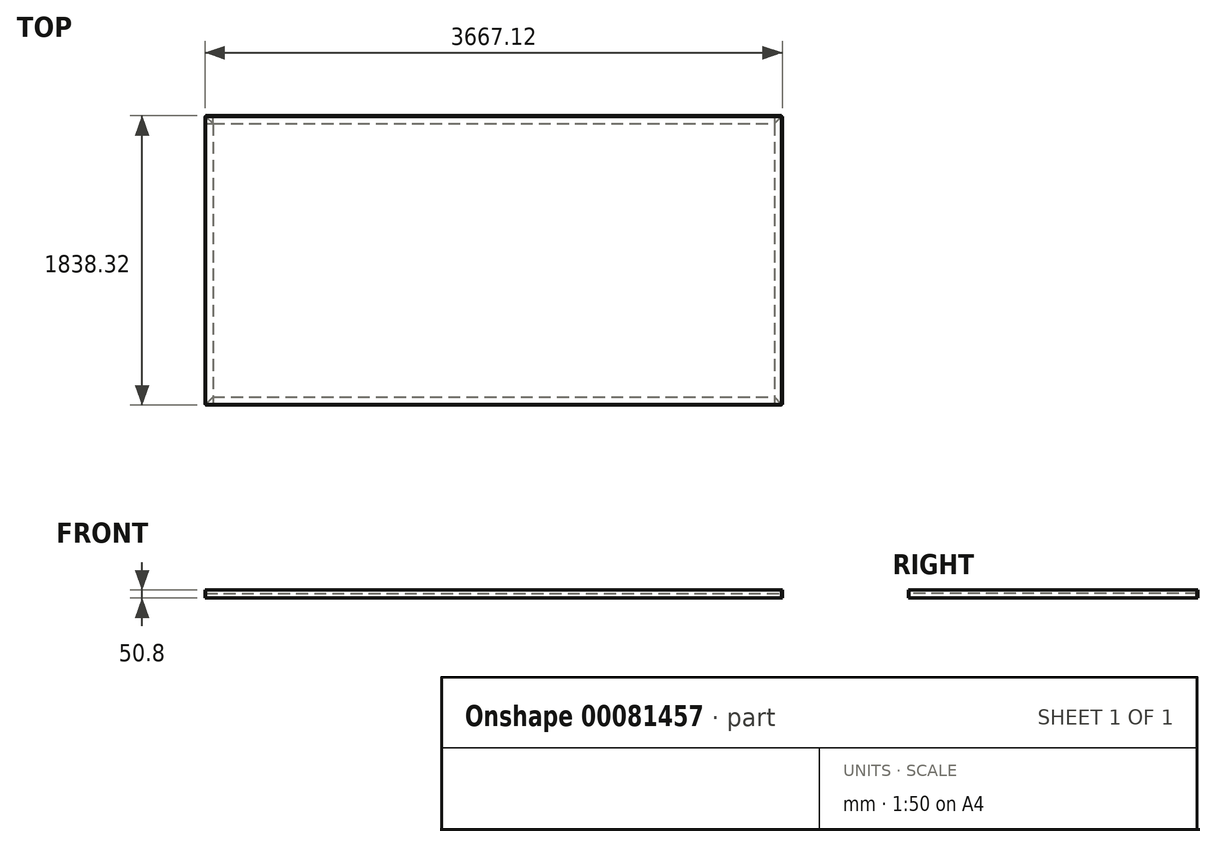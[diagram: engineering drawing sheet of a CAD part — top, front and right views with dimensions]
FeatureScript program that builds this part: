
annotation { "Feature Type Name" : "Feature", "Feature Type Description" : "" }
export const myFeature = defineFeature(function(context is Context, id is Id, definition is map)
    precondition{}
    {
        {
            var Q0;
            Q0=qCreatedBy(makeId("Right.planeOp"),FACE);
            var sketch = newSketch(context, id + "F0", { "sketchPlane" : qUnion([Q0])});
            skLineSegment(sketch, "E0.bottom", {"start": v(0, 0) * mm, "end": v(-1828.8, 0) * mm});
            skLineSegment(sketch, "E0.top", {"start": v(0, 25.4) * mm, "end": v(-1828.8, 25.4) * mm});
            skLineSegment(sketch, "E0.left", {"start": v(0, 0) * mm, "end": v(0, 25.4) * mm});
            skLineSegment(sketch, "E0.right", {"start": v(-1828.8, 0) * mm, "end": v(-1828.8, 25.4) * mm});
            skSolve(sketch);
        }
        {
            var Q0;
            Q0=makeQuery(id+"F0.imprint","IMPRINT",FACE,{"disambiguationData":[TD([[makeQuery(id+"F0.imprint","IMPRINT",EDGE,{"derivedFrom":sQuery(id+"F0.wireOp",EDGE,"E0.bottom")}),-1.0]])]});
            extrude(context, id + "F1", {"entities" : qUnion([Q0]), "oppositeDirection" : true, "depth" : 3657.6 * mm});
        }
        {
            var Q0;
            Q0=makeQuery(id+"F1.opExtrude","CAP_FACE",FACE,{"disambiguationData":[OSD([sQuery(id+"F0.wireOp",EDGE,"E0.bottom"),sQuery(id+"F0.wireOp",EDGE,"E0.top"),sQuery(id+"F0.wireOp",EDGE,"E0.left"),sQuery(id+"F0.wireOp",EDGE,"E0.right")])],"isStart":true});
            var sketch = newSketch(context, id + "F2", { "sketchPlane" : qUnion([Q0])});
            skLineSegment(sketch, "E1", {"start": v(-1828.8, 0) * mm, "end": v(-1782.76, 0) * mm});
            skLineSegment(sketch, "E2", {"start": v(-1782.76, 0) * mm, "end": v(-1782.76, -4.76) * mm});
            skLineSegment(sketch, "E3", {"start": v(-1782.76, -4.76) * mm, "end": v(-1833.56, -4.76) * mm});
            skLineSegment(sketch, "E4", {"start": v(-1833.56, -4.76) * mm, "end": v(-1833.56, 46.04) * mm});
            skLineSegment(sketch, "E5", {"start": v(-1833.56, 46.04) * mm, "end": v(-1828.8, 46.04) * mm});
            skLineSegment(sketch, "E6", {"start": v(-1828.8, 46.04) * mm, "end": v(-1828.8, 0) * mm});
            skSolve(sketch);
        }
        {
            var Q0;
            Q0 = qSketchRegion(id + "F2", true);
            var Q1;
            Q1=makeQuery(id+"F1.opExtrude","CAP_FACE",FACE,{"disambiguationData":[OSD([sQuery(id+"F0.wireOp",EDGE,"E0.bottom"),sQuery(id+"F0.wireOp",EDGE,"E0.top"),sQuery(id+"F0.wireOp",EDGE,"E0.left"),sQuery(id+"F0.wireOp",EDGE,"E0.right")])],"isStart":false});
            extrude(context, id + "F3", {"entities" : qUnion([Q0]), "endBound" : BoundingType.UP_TO_SURFACE, "oppositeDirection" : true, "endBoundEntityFace" : qUnion([Q1]), "depth" : 25.4 * mm});
        }
        {
            var Q0;
            Q0=makeQuery(id+"F1.opExtrude","CAP_FACE",FACE,{"disambiguationData":[OSD([sQuery(id+"F0.wireOp",EDGE,"E0.bottom"),sQuery(id+"F0.wireOp",EDGE,"E0.top"),sQuery(id+"F0.wireOp",EDGE,"E0.left"),sQuery(id+"F0.wireOp",EDGE,"E0.right")])],"isStart":true});
            var sketch = newSketch(context, id + "F4", { "sketchPlane" : qUnion([Q0])});
            skLineSegment(sketch, "E7", {"start": v(0, 0) * mm, "end": v(0, 46.04) * mm});
            skPoint(sketch, "E7.endSnap0", {"position": v(0, 12.7) * mm});
            skLineSegment(sketch, "E8", {"start": v(0, 46.04) * mm, "end": v(4.76, 46.04) * mm});
            skLineSegment(sketch, "E9", {"start": v(4.76, 46.04) * mm, "end": v(4.76, -4.76) * mm});
            skLineSegment(sketch, "E10", {"start": v(4.76, -4.76) * mm, "end": v(-46.04, -4.76) * mm});
            skLineSegment(sketch, "E11", {"start": v(-46.04, -4.76) * mm, "end": v(-46.04, 0) * mm});
            skLineSegment(sketch, "E12", {"start": v(-46.04, 0) * mm, "end": v(0, 0) * mm});
            skSolve(sketch);
        }
        {
            var Q0;
            Q0 = qSketchRegion(id + "F4", true);
            var Q1;
            Q1=makeQuery(id+"F1.opExtrude","CAP_FACE",FACE,{"disambiguationData":[OSD([sQuery(id+"F0.wireOp",EDGE,"E0.bottom"),sQuery(id+"F0.wireOp",EDGE,"E0.top"),sQuery(id+"F0.wireOp",EDGE,"E0.left"),sQuery(id+"F0.wireOp",EDGE,"E0.right")])],"isStart":false});
            extrude(context, id + "F5", {"entities" : qUnion([Q0]), "endBound" : BoundingType.UP_TO_SURFACE, "oppositeDirection" : true, "endBoundEntityFace" : qUnion([Q1]), "depth" : 25.4 * mm});
        }
        {
            var Q0;
            Q0=makeQuery(id+"F3.opExtrude","SWEPT_FACE",FACE,{"disambiguationData":[OSD([sQuery(id+"F2.wireOp",EDGE,"E3")])]});
            var sketch = newSketch(context, id + "F6", { "sketchPlane" : qUnion([Q0])});
            skLineSegment(sketch, "E13", {"start": v(-3657.6, 1782.76) * mm, "end": v(-3657.6, 1828.8) * mm});
            skLineSegment(sketch, "E14", {"start": v(-3657.6, 1828.8) * mm, "end": v(-3611.56, 1782.76) * mm});
            skLineSegment(sketch, "E15", {"start": v(-3611.56, 1782.76) * mm, "end": v(-3657.6, 1782.76) * mm});
            skLineSegment(sketch, "E16", {"start": v(0, 1828.8) * mm, "end": v(-46.04, 1782.76) * mm});
            skLineSegment(sketch, "E17", {"start": v(-46.04, 1782.76) * mm, "end": v(0, 1782.76) * mm});
            skLineSegment(sketch, "E18", {"start": v(0, 1782.76) * mm, "end": v(0, 1828.8) * mm});
            skSolve(sketch);
        }
        {
            var Q0;
            Q0=makeQuery(id+"F6.imprint","IMPRINT",FACE,{"disambiguationData":[TD([[makeQuery(id+"F6.imprint","IMPRINT",EDGE,{"derivedFrom":sQuery(id+"F6.wireOp",EDGE,"E16")}),1.0]])]});
            var Q1;
            Q1=makeQuery(id+"F6.imprint","IMPRINT",FACE,{"disambiguationData":[TD([[makeQuery(id+"F6.imprint","IMPRINT",EDGE,{"derivedFrom":sQuery(id+"F6.wireOp",EDGE,"E13")}),1.0]])]});
            var Q2;
            Q2=makeQuery(id+"F1.opExtrude","SWEPT_FACE",FACE,{"disambiguationData":[OSD([sQuery(id+"F0.wireOp",EDGE,"E0.bottom")])]});
            extrude(context, id + "F7", {"entities" : qUnion([Q0, Q1]), "operationType" : NewBodyOperationType.REMOVE, "endBound" : BoundingType.UP_TO_SURFACE, "oppositeDirection" : true, "endBoundEntityFace" : qUnion([Q2]), "depth" : 25.4 * mm});
        }
        {
            var Q0;
            Q0=makeQuery(id+"F1.opExtrude","SWEPT_FACE",FACE,{"disambiguationData":[OSD([sQuery(id+"F0.wireOp",EDGE,"E0.right")])]});
            var sketch = newSketch(context, id + "F8", { "sketchPlane" : qUnion([Q0])});
            skLineSegment(sketch, "E19", {"start": v(-3657.6, 0) * mm, "end": v(-3611.56, 0) * mm});
            skLineSegment(sketch, "E20", {"start": v(-3611.56, 0) * mm, "end": v(-3611.56, -4.76) * mm});
            skLineSegment(sketch, "E21", {"start": v(-3611.56, -4.76) * mm, "end": v(-3662.36, -4.76) * mm});
            skLineSegment(sketch, "E22", {"start": v(-3662.36, -4.76) * mm, "end": v(-3662.36, 46.04) * mm});
            skLineSegment(sketch, "E23", {"start": v(-3662.36, 46.04) * mm, "end": v(-3657.6, 46.04) * mm});
            skLineSegment(sketch, "E24", {"start": v(-3657.6, 46.04) * mm, "end": v(-3657.6, 0) * mm});
            skLineSegment(sketch, "E25", {"start": v(0, 0) * mm, "end": v(0, 46.04) * mm});
            skLineSegment(sketch, "E26", {"start": v(0, 46.04) * mm, "end": v(4.76, 46.04) * mm});
            skLineSegment(sketch, "E27", {"start": v(4.76, 46.04) * mm, "end": v(4.76, -4.76) * mm});
            skLineSegment(sketch, "E28", {"start": v(4.76, -4.76) * mm, "end": v(-46.04, -4.76) * mm});
            skLineSegment(sketch, "E29", {"start": v(-46.04, -4.76) * mm, "end": v(-46.04, 0) * mm});
            skLineSegment(sketch, "E30", {"start": v(-46.04, 0) * mm, "end": v(0, 0) * mm});
            skSolve(sketch);
        }
        {
            var Q0;
            {var subQ1=sQuery(id+"F8.wireOp",EDGE,"E19");Q0=makeQuery(id+"F8.imprint","IMPRINT",FACE,{"disambiguationData":[TD([[makeQuery(id+"F8.imprint","IMPRINT",EDGE,{"derivedFrom":subQ1}),-1.0]])]});}
            var Q1;
            Q1=makeQuery(id+"F1.opExtrude","SWEPT_FACE",FACE,{"disambiguationData":[OSD([sQuery(id+"F0.wireOp",EDGE,"E0.left")])]});
            extrude(context, id + "F9", {"entities" : qUnion([Q0]), "endBound" : BoundingType.UP_TO_SURFACE, "oppositeDirection" : true, "endBoundEntityFace" : qUnion([Q1]), "depth" : 25.4 * mm});
        }
        {
            var Q0;
            Q0=makeQuery(id+"F5.opExtrude","SWEPT_FACE",FACE,{"disambiguationData":[OSD([sQuery(id+"F4.wireOp",EDGE,"E10")])]});
            var sketch = newSketch(context, id + "F10", { "sketchPlane" : qUnion([Q0])});
            skLineSegment(sketch, "E31", {"start": v(0, 0) * mm, "end": v(-46.04, 46.04) * mm});
            skLineSegment(sketch, "E32", {"start": v(-46.04, 46.04) * mm, "end": v(0, 46.04) * mm});
            skLineSegment(sketch, "E33", {"start": v(0, 46.04) * mm, "end": v(0, 0) * mm});
            skLineSegment(sketch, "E34", {"start": v(-3657.6, 0) * mm, "end": v(-3611.56, 46.04) * mm});
            skLineSegment(sketch, "E35", {"start": v(-3611.56, 46.04) * mm, "end": v(-3611.56, 0) * mm});
            skLineSegment(sketch, "E36", {"start": v(-3611.56, 0) * mm, "end": v(-3657.6, 0) * mm});
            skSolve(sketch);
        }
        {
            var Q0;
            Q0=makeQuery(id+"F10.imprint","IMPRINT",FACE,{"disambiguationData":[TD([[makeQuery(id+"F10.imprint","IMPRINT",EDGE,{"derivedFrom":sQuery(id+"F10.wireOp",EDGE,"E34")}),-1.0]])]});
            var Q1;
            Q1=makeQuery(id+"F10.imprint","IMPRINT",FACE,{"disambiguationData":[TD([[makeQuery(id+"F10.imprint","IMPRINT",EDGE,{"derivedFrom":sQuery(id+"F10.wireOp",EDGE,"E31")}),-1.0]])]});
            var Q2;
            Q2=makeQuery(id+"F1.opExtrude","SWEPT_FACE",FACE,{"disambiguationData":[OSD([sQuery(id+"F0.wireOp",EDGE,"E0.bottom")])]});
            extrude(context, id + "F11", {"entities" : qUnion([Q0, Q1]), "operationType" : NewBodyOperationType.REMOVE, "endBound" : BoundingType.UP_TO_SURFACE, "oppositeDirection" : true, "endBoundEntityFace" : qUnion([Q2]), "depth" : 25.4 * mm});
        }
        {
            var Q0;
            {var subQ0=sQuery(id+"F8.wireOp",EDGE,"E26");Q0=makeQuery(id+"F8.imprint","IMPRINT",FACE,{"disambiguationData":[TD([[makeQuery(id+"F8.imprint","IMPRINT",EDGE,{"derivedFrom":subQ0}),-1.0]])]});}
            var Q1;
            Q1=makeQuery(id+"F1.opExtrude","SWEPT_FACE",FACE,{"disambiguationData":[OSD([sQuery(id+"F0.wireOp",EDGE,"E0.left")])]});
            extrude(context, id + "F12", {"entities" : qUnion([Q0]), "endBound" : BoundingType.UP_TO_SURFACE, "oppositeDirection" : true, "endBoundEntityFace" : qUnion([Q1]), "depth" : 25.4 * mm});
        }
        {
            var Q0;
            Q0=makeQuery(id+"F12.opExtrude","SWEPT_FACE",FACE,{"disambiguationData":[OSD([sQuery(id+"F8.wireOp",EDGE,"E28")])]});
            var sketch = newSketch(context, id + "F13", { "sketchPlane" : qUnion([Q0])});
            skLineSegment(sketch, "E37", {"start": v(0, 0) * mm, "end": v(-46.04, 46.04) * mm});
            skLineSegment(sketch, "E38", {"start": v(-46.04, 46.04) * mm, "end": v(-46.04, 0) * mm});
            skLineSegment(sketch, "E39", {"start": v(-46.04, 0) * mm, "end": v(0, 0) * mm});
            skLineSegment(sketch, "E40", {"start": v(0, 1828.8) * mm, "end": v(-46.04, 1782.76) * mm});
            skLineSegment(sketch, "E41", {"start": v(-46.04, 1782.76) * mm, "end": v(-46.04, 1828.8) * mm});
            skLineSegment(sketch, "E42", {"start": v(-46.04, 1828.8) * mm, "end": v(0, 1828.8) * mm});
            skSolve(sketch);
        }
        {
            var Q0;
            Q0=makeQuery(id+"F13.imprint","IMPRINT",FACE,{"disambiguationData":[TD([[makeQuery(id+"F13.imprint","IMPRINT",EDGE,{"derivedFrom":sQuery(id+"F13.wireOp",EDGE,"E40")}),-1.0]])]});
            var Q1;
            Q1=makeQuery(id+"F13.imprint","IMPRINT",FACE,{"disambiguationData":[TD([[makeQuery(id+"F13.imprint","IMPRINT",EDGE,{"derivedFrom":sQuery(id+"F13.wireOp",EDGE,"E37")}),1.0]])]});
            var Q2;
            Q2=makeQuery(id+"F1.opExtrude","SWEPT_FACE",FACE,{"disambiguationData":[OSD([sQuery(id+"F0.wireOp",EDGE,"E0.bottom")])]});
            extrude(context, id + "F14", {"entities" : qUnion([Q0, Q1]), "operationType" : NewBodyOperationType.REMOVE, "endBound" : BoundingType.UP_TO_SURFACE, "oppositeDirection" : true, "endBoundEntityFace" : qUnion([Q2]), "depth" : 25.4 * mm});
        }
    });
